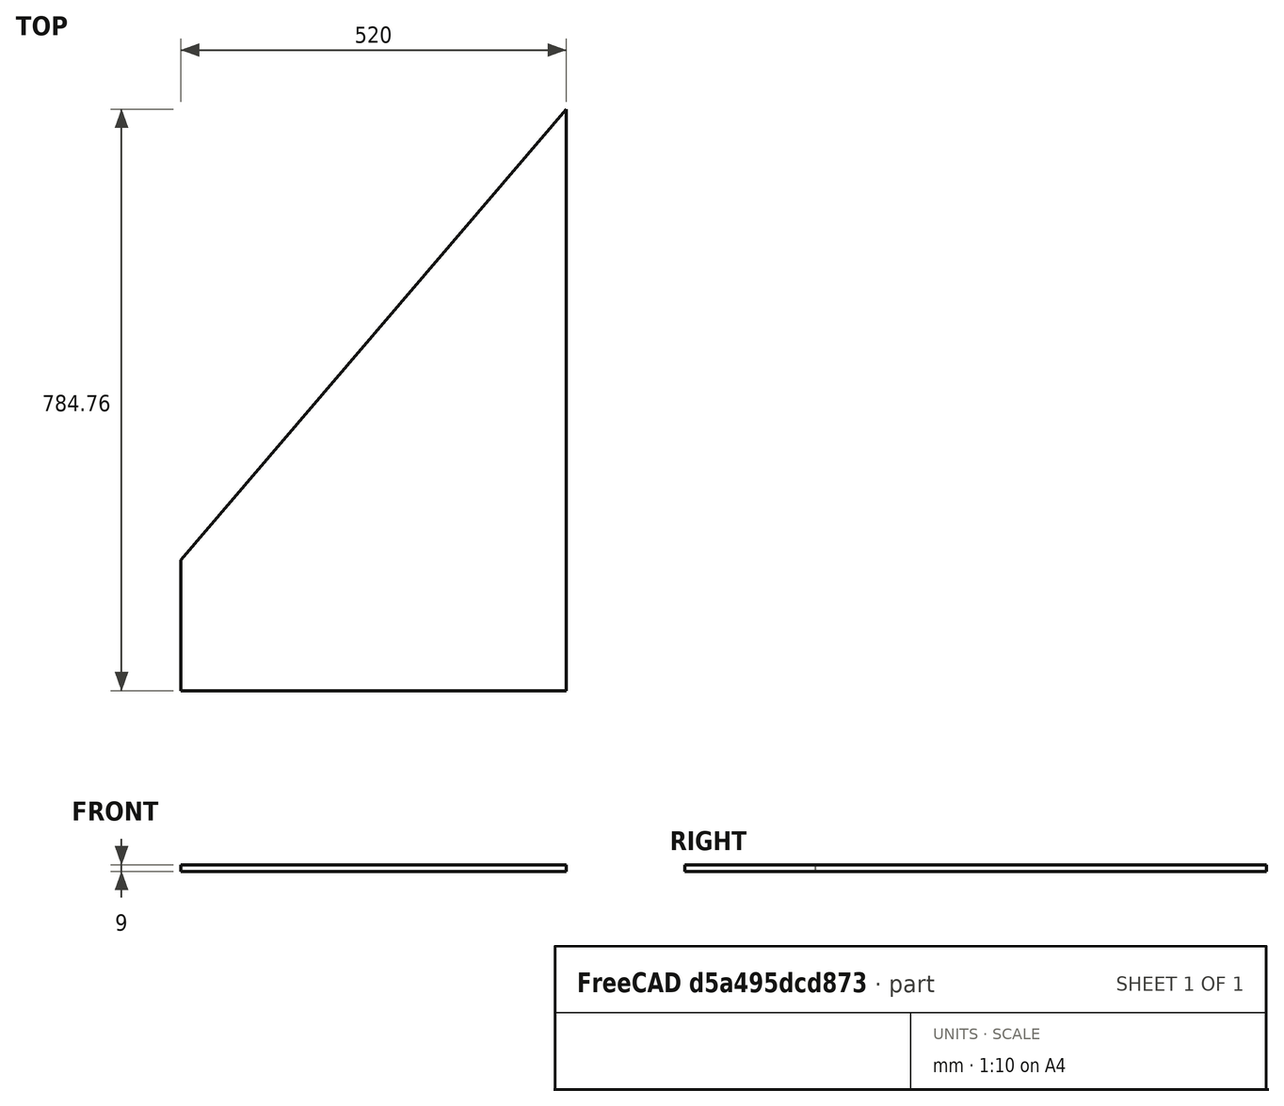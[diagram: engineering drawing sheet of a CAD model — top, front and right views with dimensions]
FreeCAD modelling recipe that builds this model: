
FCSTD DOCUMENT  (FreeCAD 1.0RUnknown)
Label: wardrobe_backplate_corpus03_jan
License: All rights reserved
LicenseURL: https://en.wikipedia.org/wiki/All_rights_reserved
objects: TechDraw::DrawViewDimension×6, PartDesign::CoordinateSystem×2, TechDraw::DrawProjGroupItem×2, Sketcher::SketchObject×1, PartDesign::Pad×1, PartDesign::Body×1, App::Part×1, TechDraw::DrawSVGTemplate×1, TechDraw::DrawPage×1
note: 16 computed .brp shape members not serialized (recipe doc carries the construction recipe); baked Part::Feature solids carry a one-line shape summary decoded from their .brp
EXTERNAL_REF file=../../mastersketch.FCStd obj=Sketch
EXTERNAL_REF file=../../mastersketch.FCStd obj=Sketch001

FEATURE [Sketcher::SketchObject] Sketch
  ArcFitTolerance = 1e-06
  AttachmentSupport = -> [XY_Plane]
  FullyConstrained = true
  MakeInternals = false
  MapMode = 5
  expr: Constraints[0] = mastersketch#<<corpus>>.Constraints.corpus03_back_height
  expr: Constraints[10] = mastersketch#Sketch.Constraints.alpha
  expr: Constraints[3] = mastersketch#Sketch.Constraints.corpus03_door_width + 5 mm
  sketch-geometry (4):
    g0: LineSegment StartX=0 StartY=0 StartZ=0 EndX=0 EndY=784.763 EndZ=0
    g1: LineSegment StartX=0 StartY=0 StartZ=0 EndX=-520 EndY=0 EndZ=0
    g2: LineSegment StartX=-520 StartY=0 StartZ=0 EndX=-520 EndY=176.309 EndZ=0
    g3: LineSegment StartX=-520 StartY=176.309 StartZ=0 EndX=0 EndY=784.763 EndZ=0
  constraints (11):
    c: Distance(g0) = 784.763
    c: Coincident(g0,g-1)
    c: Vertical(g0)
    c: Distance(g1) = 520
    c: Coincident(g1,g0)
    c: PointOnObject(g1,g-1)
    c: Vertical(g2)
    c: Coincident(g3,g2)
    c: Coincident(g2,g1)
    c: Coincident(g3,g0)
    c: Angle(g2,g3) = 2.43442
FEATURE [PartDesign::Pad] Pad
  Direction = (0,0,1)
  Length = 9
  Length2 = 10
  Profile = -> Sketch
  ReferenceAxis = -> Sketch [N_Axis]
  Refine = true
  Suppressed = false
  Type = 0
FEATURE [PartDesign::Body] Body  label="wardrobe_backplate_corpus03_jan"
  AllowCompound = false
  Group = -> [Sketch,Pad]
  Origin = -> Origin
  Tip = -> Pad
FEATURE [PartDesign::CoordinateSystem] LCS_1
  AttacherType = Attacher::AttachEngine3D
  AttachmentSupport = -> [Pad]
  MapMode = 45
  Placement = pos=(-260,0,9) rot=(0.57735,0.57735,0.57735;2.0944rad)
FEATURE [PartDesign::CoordinateSystem] LCS_Origin
  AttacherType = Attacher::AttachEngine3D
  AttachmentSupport = -> [X_Axis001]
  MapMode = 2
FEATURE [App::Part] wardrobe_backplate_corpus03_jan  label="wardrobe_backplate_corpus03_jan001"
  DrawingName = wardrobe_backplate_corpus03_jan.FCStd
  Group = -> [LCS_Origin,Body,LCS_1]
  Origin = -> Origin001
  PartDescription = wardrobe_backplate_corpus03_jan
  PartID = wardrobe_backplate_corpus03_jan
FEATURE [TechDraw::DrawSVGTemplate] Template  label="Vorlage"
  Height = 210
  Orientation = 1
  Template = <userpath>/scoop/apps/freecad/current/data/Mod/TechDraw/Templates/A4_Landscape_TD.svg
  Width = 297
FEATURE [TechDraw::DrawProjGroupItem] View
  CoarseView = false
  Direction = (0,0,-1)
  Focus = 100
  HardHidden = false
  IsoCount = 0
  IsoHidden = false
  IsoVisible = false
  LockPosition = false
  Perspective = false
  Rotation = 0
  RotationVector = (1,0,0)
  Scale = 0.1
  ScaleType = 2
  ScrubCount = 1
  SeamHidden = false
  SeamVisible = false
  SmoothHidden = false
  SmoothVisible = true
  Source = -> [wardrobe_backplate_corpus03_jan]
  Type = 0
  X = 139.342
  XDirection = (1e-16,-1,0)
  Y = 152.765
FEATURE [TechDraw::DrawProjGroupItem] View001
  CoarseView = false
  Direction = (-1,1e-16,0)
  Focus = 100
  HardHidden = false
  IsoCount = 0
  IsoHidden = false
  IsoVisible = false
  LockPosition = false
  Perspective = false
  Rotation = 0
  RotationVector = (1,0,0)
  Scale = 0.1
  ScaleType = 2
  ScrubCount = 1
  SeamHidden = false
  SeamVisible = false
  SmoothHidden = false
  SmoothVisible = true
  Source = -> [wardrobe_backplate_corpus03_jan]
  Type = 0
  X = 139.342
  XDirection = (-1e-16,-1,-1e-16)
  Y = 95.3896
FEATURE [TechDraw::DrawViewDimension] Dimension  label="Maß"
  AngleOverride = false
  Arbitrary = false
  ArbitraryTolerances = false
  BoxCorners = (2) [(-39.2381,-26,0),(39.2381,26,0)]
  EqualTolerance = true
  ExtensionAngle = 0
  FormatSpec = %.1w
  FormatSpecOverTolerance = %+.1w
  FormatSpecUnderTolerance = %+.1w
  Inverted = false
  LineAngle = 0
  LockPosition = false
  MeasureType = 1
  OverTolerance = 0
  References2D = -> [View]
  Rotation = 0
  ScaleType = 0
  TheoreticalExact = false
  Type = 2
  UnderTolerance = 0
  X = 49.6993
  Y = 0
FEATURE [TechDraw::DrawViewDimension] Dimension001  label="Maß001"
  AngleOverride = false
  Arbitrary = false
  ArbitraryTolerances = false
  BoxCorners = (2) [(-39.2381,-26,0),(39.2381,26,0)]
  EqualTolerance = true
  ExtensionAngle = 0
  FormatSpec = %.1w
  FormatSpecOverTolerance = %+.1w
  FormatSpecUnderTolerance = %+.1w
  Inverted = false
  LineAngle = 0
  LockPosition = false
  MeasureType = 1
  OverTolerance = 0
  References2D = -> [View]
  Rotation = 0
  ScaleType = 0
  TheoreticalExact = false
  Type = 1
  UnderTolerance = 0
  X = 30.4227
  Y = 41.8359
FEATURE [TechDraw::DrawViewDimension] Dimension002  label="Maß002"
  AngleOverride = false
  Arbitrary = false
  ArbitraryTolerances = false
  BoxCorners = (2) [(-39.2381,-26,0),(39.2381,26,0)]
  EqualTolerance = true
  ExtensionAngle = 0
  FormatSpec = %.1w
  FormatSpecOverTolerance = %+.1w
  FormatSpecUnderTolerance = %+.1w
  Inverted = false
  LineAngle = 0
  LockPosition = false
  MeasureType = 1
  OverTolerance = 0
  References2D = -> [View]
  Rotation = 0
  ScaleType = 0
  TheoreticalExact = false
  Type = 1
  UnderTolerance = 0
  X = 4.13456
  Y = -31.8715
FEATURE [TechDraw::DrawViewDimension] Dimension003  label="Maß003"
  AngleOverride = false
  Arbitrary = false
  ArbitraryTolerances = false
  BoxCorners = (2) [(-39.2381,-26,0),(39.2381,26,0)]
  EqualTolerance = true
  ExtensionAngle = 0
  FormatSpec = (%.1w)
  FormatSpecOverTolerance = %+.1w
  FormatSpecUnderTolerance = %+.1w
  Inverted = false
  LineAngle = 0
  LockPosition = false
  MeasureType = 1
  OverTolerance = 0
  References2D = -> [View]
  Rotation = 0
  ScaleType = 0
  TheoreticalExact = false
  Type = 6
  UnderTolerance = 0
  X = 23.687
  Y = 19.1567
FEATURE [TechDraw::DrawViewDimension] Dimension004  label="Maß004"
  AngleOverride = false
  Arbitrary = false
  ArbitraryTolerances = false
  BoxCorners = (2) [(-39.2381,-0.3,0),(39.2381,0.3,0)]
  EqualTolerance = true
  ExtensionAngle = 0
  FormatSpec = %.1w
  FormatSpecOverTolerance = %+.1w
  FormatSpecUnderTolerance = %+.1w
  Inverted = false
  LineAngle = 0
  LockPosition = false
  MeasureType = 1
  OverTolerance = 0
  References2D = -> [View001]
  Rotation = 0
  ScaleType = 0
  TheoreticalExact = false
  Type = 0
  UnderTolerance = 0
  X = 44.2586
  Y = -7.5641
FEATURE [TechDraw::DrawViewDimension] Dimension005  label="Maß005"
  AngleOverride = false
  Arbitrary = false
  ArbitraryTolerances = false
  BoxCorners = (2) [(-39.2381,-26,0),(39.2381,26,0)]
  EqualTolerance = true
  ExtensionAngle = 0
  FormatSpec = (%.2w)
  FormatSpecOverTolerance = %+.2w
  FormatSpecUnderTolerance = %+.2w
  Inverted = false
  LineAngle = 0
  LockPosition = false
  MeasureType = 1
  OverTolerance = 0
  References2D = -> [View]
  Rotation = 0
  ScaleType = 0
  TheoreticalExact = false
  Type = 0
  UnderTolerance = 0
  X = -22.0448
  Y = 15.4797
FEATURE [TechDraw::DrawPage] Page  label="Seite"
  KeepUpdated = true
  NextBalloonIndex = 1
  ProjectionType = 0
  Template = -> Template
  Views = -> [View,View001,Dimension,Dimension001,Dimension002,Dimension003,Dimension004,Dimension005]
